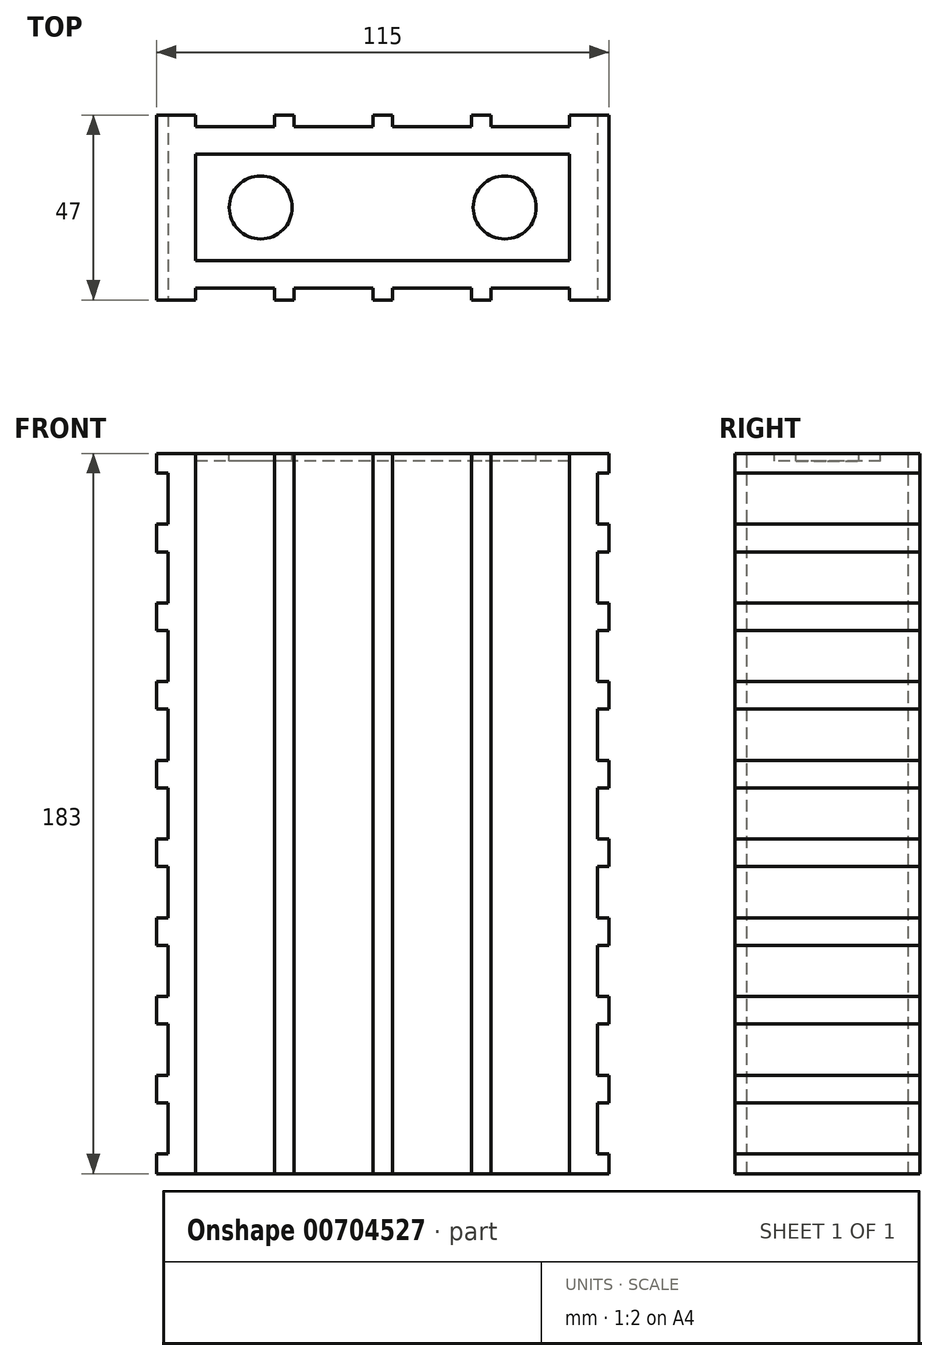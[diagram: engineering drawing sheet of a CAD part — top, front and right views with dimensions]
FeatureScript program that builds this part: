
annotation { "Feature Type Name" : "Feature", "Feature Type Description" : "" }
export const myFeature = defineFeature(function(context is Context, id is Id, definition is map)
    precondition{}
    {
        {
            var Q0;
            Q0=qCreatedBy(makeId("Top.planeOp"),FACE);
            var sketch = newSketch(context, id + "F0", { "sketchPlane" : qUnion([Q0])});
            skLineSegment(sketch, "E0.bottom", {"start": v(57.5, 23.5) * mm, "end": v(-57.5, 23.5) * mm});
            skLineSegment(sketch, "E0.top", {"start": v(57.5, -23.5) * mm, "end": v(-57.5, -23.5) * mm});
            skLineSegment(sketch, "E0.left", {"start": v(57.5, 23.5) * mm, "end": v(57.5, -23.5) * mm});
            skLineSegment(sketch, "E0.right", {"start": v(-57.5, 23.5) * mm, "end": v(-57.5, -23.5) * mm});
            skPoint(sketch, "E0.middle", {"position": v(0, 0) * mm});
            skSolve(sketch);
        }
        {
            var Q0;
            Q0 = qSketchRegion(id + "F0", true);
            extrude(context, id + "F1", {"entities" : qUnion([Q0]), "depth" : 183 * mm, "offsetDistance" : 25 * mm});
        }
        {
            var Q0;
            Q0=makeQuery(id+"F1.opExtrude","CAP_FACE",FACE,{"disambiguationData":[OSD([sQuery(id+"F0.wireOp",EDGE,"E0.bottom"),sQuery(id+"F0.wireOp",EDGE,"E0.top"),sQuery(id+"F0.wireOp",EDGE,"E0.left"),sQuery(id+"F0.wireOp",EDGE,"E0.right")])],"isStart":false});
            var sketch = newSketch(context, id + "F2", { "sketchPlane" : qUnion([Q0])});
            skLineSegment(sketch, "E1.bottom", {"start": v(47.5, 13.5) * mm, "end": v(-47.5, 13.5) * mm});
            skLineSegment(sketch, "E1.top", {"start": v(47.5, -13.5) * mm, "end": v(-47.5, -13.5) * mm});
            skLineSegment(sketch, "E1.left", {"start": v(47.5, 13.5) * mm, "end": v(47.5, -13.5) * mm});
            skLineSegment(sketch, "E1.right", {"start": v(-47.5, 13.5) * mm, "end": v(-47.5, -13.5) * mm});
            skPoint(sketch, "E1.middle", {"position": v(0, 0) * mm});
            skLineSegment(sketch, "E2", {"start": v(-31, 0) * mm, "end": v(31, 0) * mm, "construction": true});
            skCircle(sketch, "E3", {"center": v(-31, 0) * mm, "radius": 8 * mm});
            skCircle(sketch, "E4", {"center": v(31, 0) * mm, "radius": 8 * mm});
            skSolve(sketch);
        }
        {
            var Q0;
            Q0 = qSketchRegion(id + "F2", true);
            extrude(context, id + "F3", {"entities" : qUnion([Q0]), "operationType" : NewBodyOperationType.REMOVE, "oppositeDirection" : true, "depth" : 2 * mm, "offsetDistance" : 25 * mm});
        }
        {
            var Q0;
            {var subQ0=sQuery(id+"F0.wireOp",EDGE,"E0.left");var subQ1=sQuery(id+"F0.wireOp",EDGE,"E0.top");var subQ2=sQuery(id+"F0.wireOp",EDGE,"E0.right");var subQ3=sQuery(id+"F0.wireOp",EDGE,"E0.bottom");Q0=makeQuery(id+"F3.boolean.opBoolean","SPLIT",FACE,{"disambiguationData":[TD([makeQuery(id+"F1.opExtrude","SWEPT_FACE",FACE,{"disambiguationData":[OSD([subQ3])]})])],"derivedFrom":makeQuery(id+"F1.opExtrude","CAP_FACE",FACE,{"disambiguationData":[OSD([subQ3,subQ1,subQ0,subQ2])],"isStart":false})});}
            var sketch = newSketch(context, id + "F4", { "sketchPlane" : qUnion([Q0])});
            skLineSegment(sketch, "E5.bottom", {"start": v(-47.5, 23.5) * mm, "end": v(-27.5, 23.5) * mm});
            skLineSegment(sketch, "E5.top", {"start": v(-47.5, 20.5) * mm, "end": v(-27.5, 20.5) * mm});
            skLineSegment(sketch, "E5.left", {"start": v(-47.5, 23.5) * mm, "end": v(-47.5, 20.5) * mm});
            skLineSegment(sketch, "E5.right", {"start": v(-27.5, 23.5) * mm, "end": v(-27.5, 20.5) * mm});
            skLineSegment(sketch, "E6.bottom", {"start": v(-22.5, 23.5) * mm, "end": v(-2.5, 23.5) * mm});
            skLineSegment(sketch, "E6.top", {"start": v(-22.5, 20.5) * mm, "end": v(-2.5, 20.5) * mm});
            skLineSegment(sketch, "E6.left", {"start": v(-22.5, 23.5) * mm, "end": v(-22.5, 20.5) * mm});
            skLineSegment(sketch, "E6.right", {"start": v(-2.5, 23.5) * mm, "end": v(-2.5, 20.5) * mm});
            skLineSegment(sketch, "E7.bottom", {"start": v(2.5, 23.5) * mm, "end": v(22.5, 23.5) * mm});
            skLineSegment(sketch, "E7.top", {"start": v(2.5, 20.5) * mm, "end": v(22.5, 20.5) * mm});
            skLineSegment(sketch, "E7.left", {"start": v(2.5, 23.5) * mm, "end": v(2.5, 20.5) * mm});
            skLineSegment(sketch, "E7.right", {"start": v(22.5, 23.5) * mm, "end": v(22.5, 20.5) * mm});
            skLineSegment(sketch, "E8.bottom", {"start": v(27.5, 23.5) * mm, "end": v(47.5, 23.5) * mm});
            skLineSegment(sketch, "E8.top", {"start": v(27.5, 20.5) * mm, "end": v(47.5, 20.5) * mm});
            skLineSegment(sketch, "E8.left", {"start": v(27.5, 23.5) * mm, "end": v(27.5, 20.5) * mm});
            skLineSegment(sketch, "E8.right", {"start": v(47.5, 23.5) * mm, "end": v(47.5, 20.5) * mm});
            skLineSegment(sketch, "E9", {"start": v(-57.5, 0) * mm, "end": v(57.5, 0) * mm, "construction": true});
            skLineSegment(sketch, "E10.MirrorCS", {"start": v(27.5, -23.5) * mm, "end": v(27.5, -20.5) * mm});
            skLineSegment(sketch, "E11.MirrorCS", {"start": v(22.5, -23.5) * mm, "end": v(22.5, -20.5) * mm});
            skLineSegment(sketch, "E12.MirrorCS", {"start": v(-22.5, -23.5) * mm, "end": v(-22.5, -20.5) * mm});
            skLineSegment(sketch, "E13.MirrorCS", {"start": v(-2.5, -23.5) * mm, "end": v(-2.5, -20.5) * mm});
            skLineSegment(sketch, "E14.MirrorCS", {"start": v(-27.5, -23.5) * mm, "end": v(-27.5, -20.5) * mm});
            skLineSegment(sketch, "E15.MirrorCS", {"start": v(-47.5, -23.5) * mm, "end": v(-47.5, -20.5) * mm});
            skLineSegment(sketch, "E16.MirrorCS", {"start": v(47.5, -23.5) * mm, "end": v(47.5, -20.5) * mm});
            skLineSegment(sketch, "E17.MirrorCS", {"start": v(2.5, -23.5) * mm, "end": v(2.5, -20.5) * mm});
            skLineSegment(sketch, "E18.MirrorCS", {"start": v(27.5, -20.5) * mm, "end": v(47.5, -20.5) * mm});
            skLineSegment(sketch, "E19.MirrorCS", {"start": v(27.5, -23.5) * mm, "end": v(47.5, -23.5) * mm});
            skLineSegment(sketch, "E20.MirrorCS", {"start": v(-22.5, -23.5) * mm, "end": v(-2.5, -23.5) * mm});
            skLineSegment(sketch, "E21.MirrorCS", {"start": v(-22.5, -20.5) * mm, "end": v(-2.5, -20.5) * mm});
            skLineSegment(sketch, "E22.MirrorCS", {"start": v(2.5, -23.5) * mm, "end": v(22.5, -23.5) * mm});
            skLineSegment(sketch, "E23.MirrorCS", {"start": v(-47.5, -20.5) * mm, "end": v(-27.5, -20.5) * mm});
            skLineSegment(sketch, "E24.MirrorCS", {"start": v(-47.5, -23.5) * mm, "end": v(-27.5, -23.5) * mm});
            skLineSegment(sketch, "E25.MirrorCS", {"start": v(2.5, -20.5) * mm, "end": v(22.5, -20.5) * mm});
            skSolve(sketch);
        }
        {
            var Q0;
            Q0 = qSketchRegion(id + "F4", true);
            extrude(context, id + "F5", {"entities" : qUnion([Q0]), "operationType" : NewBodyOperationType.REMOVE, "endBound" : BoundingType.THROUGH_ALL, "oppositeDirection" : true, "depth" : 25 * mm, "offsetDistance" : 25 * mm});
        }
        {
            var Q0;
            {var subQ0=sQuery(id+"F0.wireOp",EDGE,"E0.right");var subQ2=sQuery(id+"F0.wireOp",EDGE,"E0.top");Q0=makeQuery(id+"F5.boolean.opBoolean","SPLIT",FACE,{"disambiguationData":[TD([makeQuery(id+"F1.opExtrude","SWEPT_FACE",FACE,{"disambiguationData":[OSD([subQ0])]})])],"derivedFrom":makeQuery(id+"F1.opExtrude","SWEPT_FACE",FACE,{"disambiguationData":[OSD([subQ2])]})});}
            var sketch = newSketch(context, id + "F6", { "sketchPlane" : qUnion([Q0])});
            skLineSegment(sketch, "E26.bottom", {"start": v(-57.5, 178) * mm, "end": v(-54.5, 178) * mm});
            skLineSegment(sketch, "E26.top", {"start": v(-57.5, 165) * mm, "end": v(-54.5, 165) * mm});
            skLineSegment(sketch, "E26.left", {"start": v(-57.5, 178) * mm, "end": v(-57.5, 165) * mm});
            skLineSegment(sketch, "E26.right", {"start": v(-54.5, 178) * mm, "end": v(-54.5, 165) * mm});
            skLineSegment(sketch, "E27.0.1.0", {"start": v(-57.5, 158) * mm, "end": v(-54.5, 158) * mm});
            skLineSegment(sketch, "E27.0.1.1", {"start": v(-57.5, 145) * mm, "end": v(-54.5, 145) * mm});
            skLineSegment(sketch, "E27.0.1.2", {"start": v(-57.5, 158) * mm, "end": v(-57.5, 145) * mm});
            skLineSegment(sketch, "E27.0.1.3", {"start": v(-54.5, 158) * mm, "end": v(-54.5, 145) * mm});
            skLineSegment(sketch, "E27.0.2.0", {"start": v(-57.5, 138) * mm, "end": v(-54.5, 138) * mm});
            skLineSegment(sketch, "E27.0.2.1", {"start": v(-57.5, 125) * mm, "end": v(-54.5, 125) * mm});
            skLineSegment(sketch, "E27.0.2.2", {"start": v(-57.5, 138) * mm, "end": v(-57.5, 125) * mm});
            skLineSegment(sketch, "E27.0.2.3", {"start": v(-54.5, 138) * mm, "end": v(-54.5, 125) * mm});
            skLineSegment(sketch, "E27.0.3.0", {"start": v(-57.5, 118) * mm, "end": v(-54.5, 118) * mm});
            skLineSegment(sketch, "E27.0.3.1", {"start": v(-57.5, 105) * mm, "end": v(-54.5, 105) * mm});
            skLineSegment(sketch, "E27.0.3.2", {"start": v(-57.5, 118) * mm, "end": v(-57.5, 105) * mm});
            skLineSegment(sketch, "E27.0.3.3", {"start": v(-54.5, 118) * mm, "end": v(-54.5, 105) * mm});
            skLineSegment(sketch, "E27.0.4.0", {"start": v(-57.5, 98) * mm, "end": v(-54.5, 98) * mm});
            skLineSegment(sketch, "E27.0.4.1", {"start": v(-57.5, 85) * mm, "end": v(-54.5, 85) * mm});
            skLineSegment(sketch, "E27.0.4.2", {"start": v(-57.5, 98) * mm, "end": v(-57.5, 85) * mm});
            skLineSegment(sketch, "E27.0.4.3", {"start": v(-54.5, 98) * mm, "end": v(-54.5, 85) * mm});
            skLineSegment(sketch, "E27.0.5.0", {"start": v(-57.5, 78) * mm, "end": v(-54.5, 78) * mm});
            skLineSegment(sketch, "E27.0.5.1", {"start": v(-57.5, 65) * mm, "end": v(-54.5, 65) * mm});
            skLineSegment(sketch, "E27.0.5.2", {"start": v(-57.5, 78) * mm, "end": v(-57.5, 65) * mm});
            skLineSegment(sketch, "E27.0.5.3", {"start": v(-54.5, 78) * mm, "end": v(-54.5, 65) * mm});
            skLineSegment(sketch, "E27.0.6.0", {"start": v(-57.5, 58) * mm, "end": v(-54.5, 58) * mm});
            skLineSegment(sketch, "E27.0.6.1", {"start": v(-57.5, 45) * mm, "end": v(-54.5, 45) * mm});
            skLineSegment(sketch, "E27.0.6.2", {"start": v(-57.5, 58) * mm, "end": v(-57.5, 45) * mm});
            skLineSegment(sketch, "E27.0.6.3", {"start": v(-54.5, 58) * mm, "end": v(-54.5, 45) * mm});
            skLineSegment(sketch, "E27.0.7.0", {"start": v(-57.5, 38) * mm, "end": v(-54.5, 38) * mm});
            skLineSegment(sketch, "E27.0.7.1", {"start": v(-57.5, 25) * mm, "end": v(-54.5, 25) * mm});
            skLineSegment(sketch, "E27.0.7.2", {"start": v(-57.5, 38) * mm, "end": v(-57.5, 25) * mm});
            skLineSegment(sketch, "E27.0.7.3", {"start": v(-54.5, 38) * mm, "end": v(-54.5, 25) * mm});
            skLineSegment(sketch, "E27.0.8.0", {"start": v(-57.5, 18) * mm, "end": v(-54.5, 18) * mm});
            skLineSegment(sketch, "E27.0.8.1", {"start": v(-57.5, 5) * mm, "end": v(-54.5, 5) * mm});
            skLineSegment(sketch, "E27.0.8.2", {"start": v(-57.5, 18) * mm, "end": v(-57.5, 5) * mm});
            skLineSegment(sketch, "E27.0.8.3", {"start": v(-54.5, 18) * mm, "end": v(-54.5, 5) * mm});
            skLineSegment(sketch, "E27.direction1", {"start": v(-57.5, 165) * mm, "end": v(-32.5, 165) * mm, "construction": true});
            skLineSegment(sketch, "E27.direction2", {"start": v(-57.5, 165) * mm, "end": v(-57.5, 145) * mm, "construction": true});
            skLineSegment(sketch, "E28", {"start": v(0, 0) * mm, "end": v(0, 189.57) * mm, "construction": true});
            skLineSegment(sketch, "E29.MirrorCS", {"start": v(57.5, 165) * mm, "end": v(54.5, 165) * mm});
            skLineSegment(sketch, "E30.MirrorCS", {"start": v(57.5, 145) * mm, "end": v(54.5, 145) * mm});
            skLineSegment(sketch, "E31.MirrorCS", {"start": v(57.5, 178) * mm, "end": v(54.5, 178) * mm});
            skLineSegment(sketch, "E32.MirrorCS", {"start": v(57.5, 158) * mm, "end": v(54.5, 158) * mm});
            skLineSegment(sketch, "E33.MirrorCS", {"start": v(57.5, 138) * mm, "end": v(54.5, 138) * mm});
            skLineSegment(sketch, "E34.MirrorCS", {"start": v(57.5, 125) * mm, "end": v(54.5, 125) * mm});
            skLineSegment(sketch, "E35.MirrorCS", {"start": v(57.5, 118) * mm, "end": v(54.5, 118) * mm});
            skLineSegment(sketch, "E36.MirrorCS", {"start": v(57.5, 85) * mm, "end": v(54.5, 85) * mm});
            skLineSegment(sketch, "E37.MirrorCS", {"start": v(57.5, 5) * mm, "end": v(54.5, 5) * mm});
            skLineSegment(sketch, "E38.MirrorCS", {"start": v(57.5, 58) * mm, "end": v(54.5, 58) * mm});
            skLineSegment(sketch, "E39.MirrorCS", {"start": v(57.5, 45) * mm, "end": v(54.5, 45) * mm});
            skLineSegment(sketch, "E40.MirrorCS", {"start": v(57.5, 78) * mm, "end": v(54.5, 78) * mm});
            skLineSegment(sketch, "E41.MirrorCS", {"start": v(57.5, 25) * mm, "end": v(54.5, 25) * mm});
            skLineSegment(sketch, "E42.MirrorCS", {"start": v(57.5, 38) * mm, "end": v(54.5, 38) * mm});
            skLineSegment(sketch, "E43.MirrorCS", {"start": v(57.5, 65) * mm, "end": v(54.5, 65) * mm});
            skLineSegment(sketch, "E44.MirrorCS", {"start": v(57.5, 105) * mm, "end": v(54.5, 105) * mm});
            skLineSegment(sketch, "E45.MirrorCS", {"start": v(57.5, 98) * mm, "end": v(54.5, 98) * mm});
            skLineSegment(sketch, "E46.MirrorCS", {"start": v(57.5, 18) * mm, "end": v(54.5, 18) * mm});
            skLineSegment(sketch, "E47.MirrorCS", {"start": v(57.5, 158) * mm, "end": v(57.5, 145) * mm});
            skLineSegment(sketch, "E48.MirrorCS", {"start": v(57.5, 118) * mm, "end": v(57.5, 105) * mm});
            skLineSegment(sketch, "E49.MirrorCS", {"start": v(57.5, 178) * mm, "end": v(57.5, 165) * mm});
            skLineSegment(sketch, "E50.MirrorCS", {"start": v(54.5, 178) * mm, "end": v(54.5, 165) * mm});
            skLineSegment(sketch, "E51.MirrorCS", {"start": v(54.5, 118) * mm, "end": v(54.5, 105) * mm});
            skLineSegment(sketch, "E52.MirrorCS", {"start": v(54.5, 158) * mm, "end": v(54.5, 145) * mm});
            skLineSegment(sketch, "E53.MirrorCS", {"start": v(54.5, 78) * mm, "end": v(54.5, 65) * mm});
            skLineSegment(sketch, "E54.MirrorCS", {"start": v(57.5, 138) * mm, "end": v(57.5, 125) * mm});
            skLineSegment(sketch, "E55.MirrorCS", {"start": v(54.5, 138) * mm, "end": v(54.5, 125) * mm});
            skLineSegment(sketch, "E56.MirrorCS", {"start": v(57.5, 18) * mm, "end": v(57.5, 5) * mm});
            skLineSegment(sketch, "E57.MirrorCS", {"start": v(57.5, 98) * mm, "end": v(57.5, 85) * mm});
            skLineSegment(sketch, "E58.MirrorCS", {"start": v(57.5, 58) * mm, "end": v(57.5, 45) * mm});
            skLineSegment(sketch, "E59.MirrorCS", {"start": v(54.5, 98) * mm, "end": v(54.5, 85) * mm});
            skLineSegment(sketch, "E60.MirrorCS", {"start": v(54.5, 18) * mm, "end": v(54.5, 5) * mm});
            skLineSegment(sketch, "E61.MirrorCS", {"start": v(54.5, 58) * mm, "end": v(54.5, 45) * mm});
            skLineSegment(sketch, "E62.MirrorCS", {"start": v(57.5, 38) * mm, "end": v(57.5, 25) * mm});
            skLineSegment(sketch, "E63.MirrorCS", {"start": v(57.5, 165) * mm, "end": v(57.5, 145) * mm, "construction": true});
            skLineSegment(sketch, "E64.MirrorCS", {"start": v(57.5, 78) * mm, "end": v(57.5, 65) * mm});
            skLineSegment(sketch, "E65.MirrorCS", {"start": v(54.5, 38) * mm, "end": v(54.5, 25) * mm});
            skSolve(sketch);
        }
        {
            var Q0;
            Q0 = qSketchRegion(id + "F6", true);
            extrude(context, id + "F7", {"entities" : qUnion([Q0]), "operationType" : NewBodyOperationType.REMOVE, "endBound" : BoundingType.THROUGH_ALL, "oppositeDirection" : true, "depth" : 25 * mm, "offsetDistance" : 25 * mm});
        }
    });
